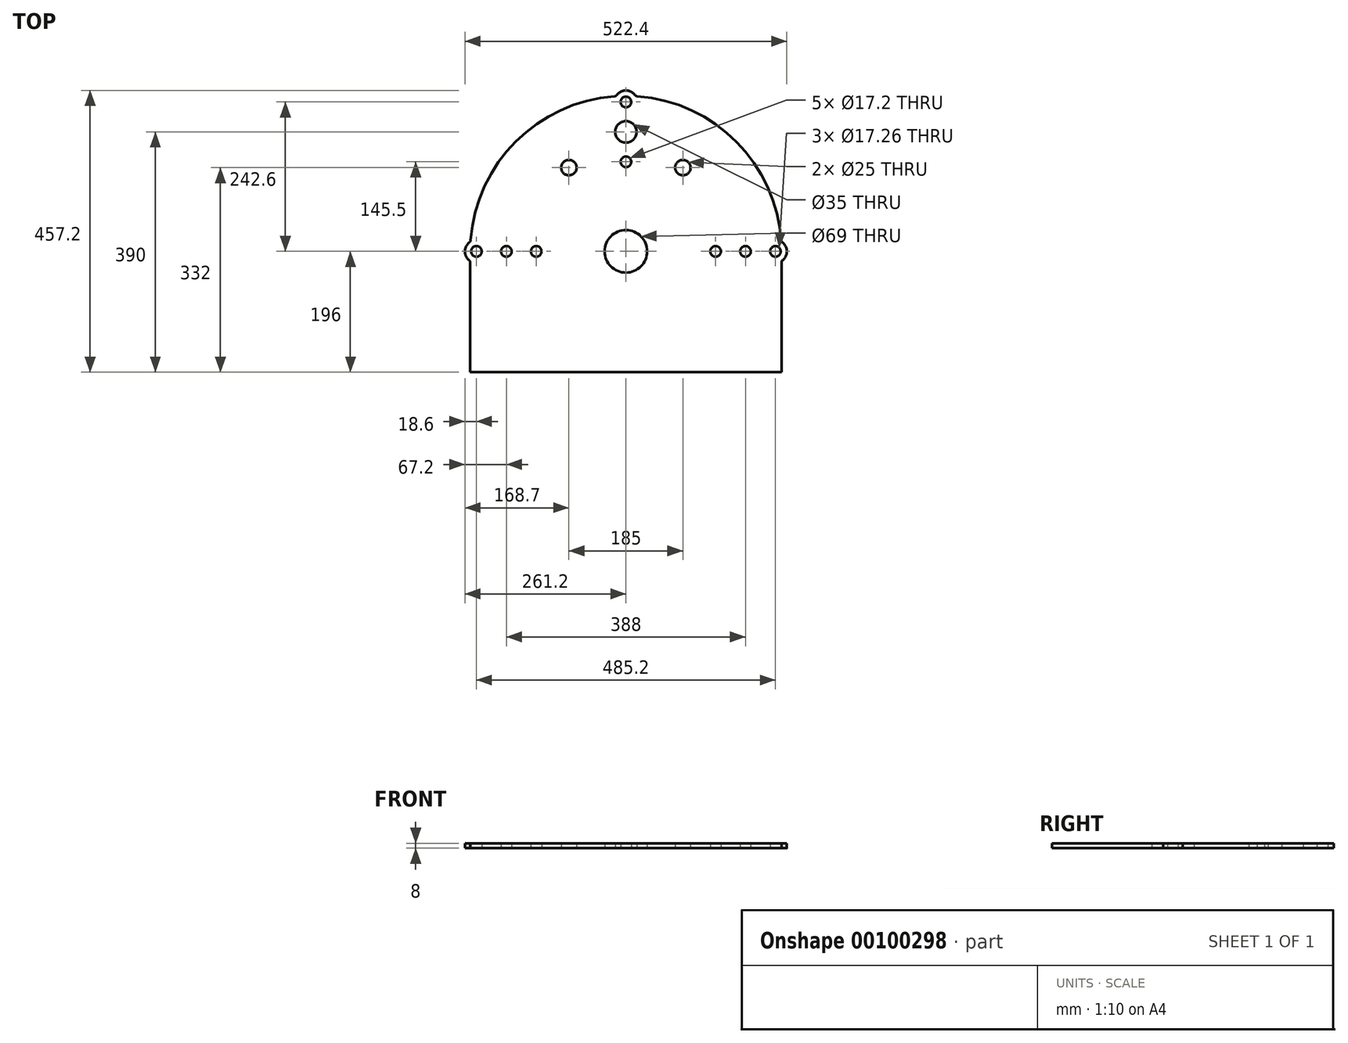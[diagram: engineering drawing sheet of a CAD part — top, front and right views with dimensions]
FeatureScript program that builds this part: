
annotation { "Feature Type Name" : "Feature", "Feature Type Description" : "" }
export const myFeature = defineFeature(function(context is Context, id is Id, definition is map)
    precondition{}
    {
        {
            var Q0;
            Q0=qCreatedBy(makeId("Top.planeOp"),FACE);
            var sketch = newSketch(context, id + "F0", { "sketchPlane" : qUnion([Q0])});
            skArc(sketch, "E0", {"start": v(14.85, 221.2) * mm, "mid": v(16.45, 219.82) * mm, "end": v(18.48, 219.22) * mm});
            skArc(sketch, "E1", {"start": v(-18.48, 219.22) * mm, "mid": v(-16.45, 219.82) * mm, "end": v(-14.85, 221.2) * mm});
            skArc(sketch, "E2", {"start": v(-253.8, -17.75) * mm, "mid": v(-252.42, -16.15) * mm, "end": v(-251.82, -14.12) * mm});
            skArc(sketch, "E3", {"start": v(-252.5, -50.9) * mm, "mid": v(-252.98, -48.76) * mm, "end": v(-254.34, -47.02) * mm});
            skArc(sketch, "E4", {"start": v(251.99, -16.54) * mm, "mid": v(179.4, 145.08) * mm, "end": v(18.48, 219.22) * mm});
            skArc(sketch, "E5", {"start": v(14.85, 221.2) * mm, "mid": v(0, 228.6) * mm, "end": v(-14.85, 221.2) * mm});
            skArc(sketch, "E6", {"start": v(-18.48, 219.22) * mm, "mid": v(-178.54, 145.94) * mm, "end": v(-251.82, -14.12) * mm});
            skArc(sketch, "E7", {"start": v(-253.8, -17.75) * mm, "mid": v(-261.2, -32.25) * mm, "end": v(-254.34, -47.02) * mm});
            skLineSegment(sketch, "E8", {"start": v(-252.5, -50.9) * mm, "end": v(-252.5, -228.6) * mm});
            skArc(sketch, "E9", {"start": v(252.5, -48.35) * mm, "mid": v(261.2, -32.3) * mm, "end": v(251.99, -16.54) * mm});
            skLineSegment(sketch, "E10", {"start": v(252.5, -228.6) * mm, "end": v(252.5, -48.35) * mm});
            skLineSegment(sketch, "E11", {"start": v(252.5, -228.6) * mm, "end": v(-252.5, -228.6) * mm});
            skCircle(sketch, "E12", {"center": v(-194, -32.6) * mm, "radius": 8.6 * mm});
            skCircle(sketch, "E13", {"center": v(145.5, -32.6) * mm, "radius": 8.6 * mm});
            skCircle(sketch, "E14", {"center": v(194, -32.6) * mm, "radius": 8.6 * mm});
            skCircle(sketch, "E15", {"center": v(0, 112.9) * mm, "radius": 8.6 * mm});
            skCircle(sketch, "E16", {"center": v(-145.5, -32.6) * mm, "radius": 8.6 * mm});
            skCircle(sketch, "E17", {"center": v(92.5, 103.4) * mm, "radius": 12.5 * mm});
            skCircle(sketch, "E18", {"center": v(-92.5, 103.4) * mm, "radius": 12.5 * mm});
            skCircle(sketch, "E19", {"center": v(242.6, -32.6) * mm, "radius": 8.63 * mm});
            skCircle(sketch, "E20", {"center": v(0, 210) * mm, "radius": 8.63 * mm});
            skCircle(sketch, "E21", {"center": v(-242.6, -32.6) * mm, "radius": 8.63 * mm});
            skCircle(sketch, "E22", {"center": v(0, 161.4) * mm, "radius": 17.5 * mm});
            skCircle(sketch, "E23", {"center": v(0, -32.6) * mm, "radius": 34.5 * mm});
            skSolve(sketch);
        }
        {
            var Q0;
            Q0=qSketchRegion(id+"F0",true);
            extrude(context, id + "F1", {"entities" : qUnion([Q0]), "depth" : 8 * mm});
        }
    });
